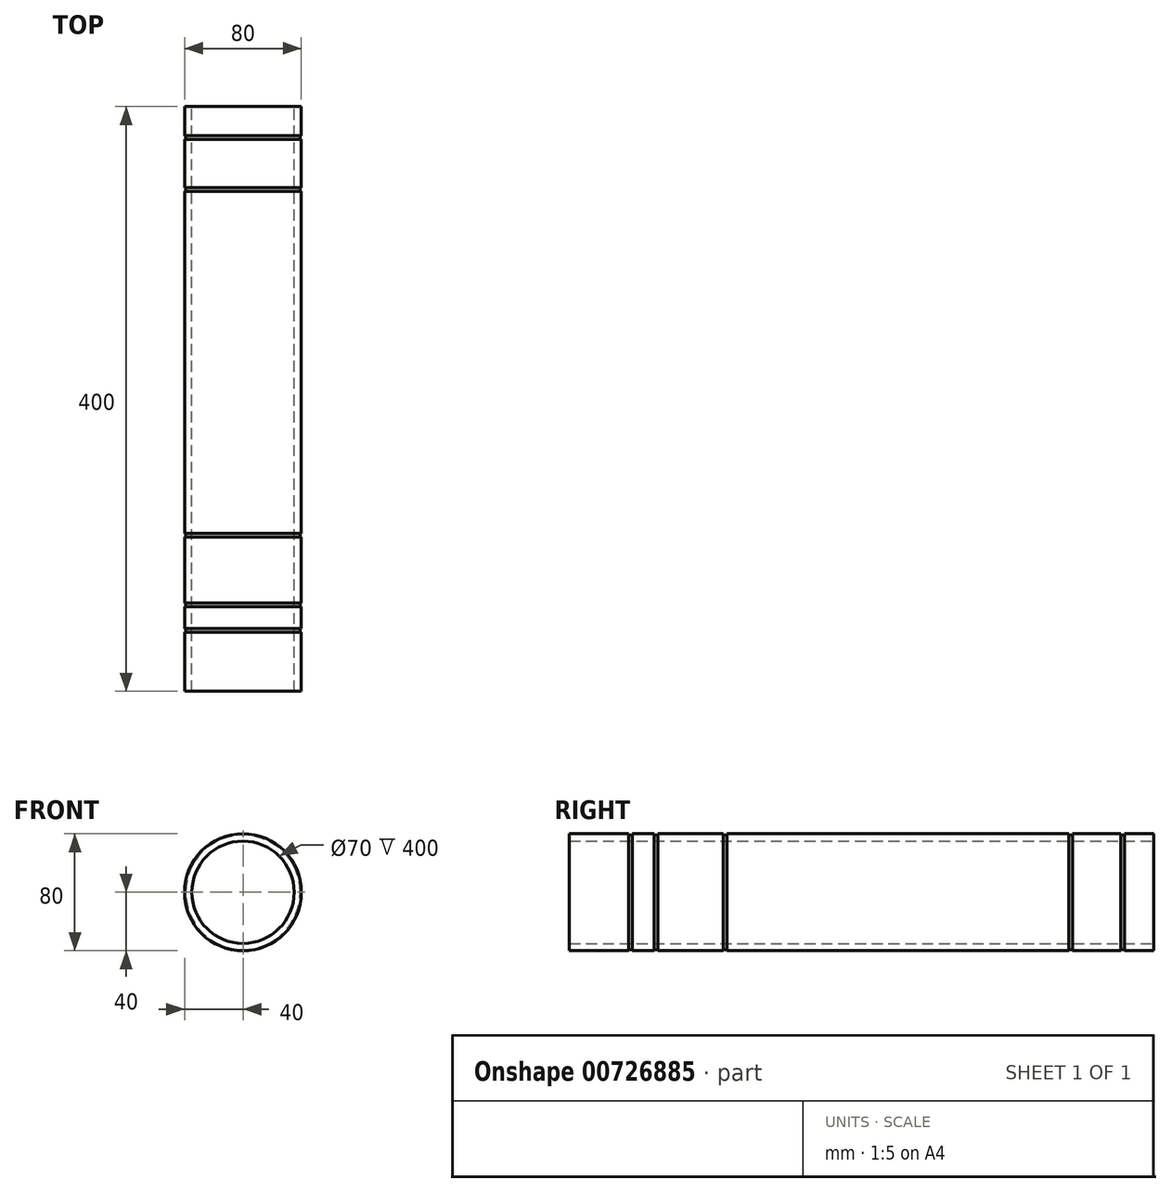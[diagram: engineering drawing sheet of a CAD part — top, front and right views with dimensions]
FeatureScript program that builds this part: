
annotation { "Feature Type Name" : "Feature", "Feature Type Description" : "" }
export const myFeature = defineFeature(function(context is Context, id is Id, definition is map)
    precondition{}
    {
        {
            var Q0;
            Q0=qCreatedBy(makeId("Front.planeOp"),FACE);
            var sketch = newSketch(context, id + "F0", { "sketchPlane" : qUnion([Q0])});
            skCircle(sketch, "E0", {"center": v(0, 0) * mm, "radius": 40 * mm});
            skCircle(sketch, "E1", {"center": v(0, 0) * mm, "radius": 35 * mm});
            skSolve(sketch);
        }
        {
            var Q0;
            Q0=makeQuery(id+"F0.imprint","IMPRINT",FACE,{"disambiguationData":[TD([[makeQuery(id+"F0.imprint","IMPRINT",EDGE,{"derivedFrom":sQuery(id+"F0.wireOp",EDGE,"E0")}),1.0]])]});
            extrude(context, id + "F1", {"entities" : qUnion([Q0]), "depth" : 400 * mm, "offsetDistance" : 25 * mm});
        }
        {
            var Q0;
            Q0=qCreatedBy(makeId("Front.planeOp"),FACE);
            cPlane(context, id + "F2", {"entities" : qUnion([Q0]), "cplaneType" : CPlaneType.OFFSET, "offset" : 20 * mm, "width" : 150 * mm, "height" : 150 * mm});
        }
        {
            var Q0;
            Q0=qCreatedBy(id+"F2.planeOp",FACE);
            var sketch = newSketch(context, id + "F3", { "sketchPlane" : qUnion([Q0])});
            skCircle(sketch, "E2", {"center": v(0, 0) * mm, "radius": 39.15 * mm});
            skCircle(sketch, "E3", {"center": v(0, 0) * mm, "radius": 44 * mm});
            skSolve(sketch);
        }
        {
            var Q0;
            Q0=qSketchRegion(id+"F3",true);
            extrude(context, id + "F4", {"entities" : qUnion([Q0]), "operationType" : NewBodyOperationType.REMOVE, "depth" : 2.5 * mm, "offsetDistance" : 25 * mm});
        }
        {
            var Q0;
            Q0=qCreatedBy(id+"F2.planeOp",FACE);
            cPlane(context, id + "F5", {"entities" : qUnion([Q0]), "cplaneType" : CPlaneType.OFFSET, "offset" : 35.5 * mm, "width" : 150 * mm, "height" : 150 * mm});
        }
        {
            var Q0;
            Q0=qCreatedBy(id+"F5.planeOp",FACE);
            var sketch = newSketch(context, id + "F6", { "sketchPlane" : qUnion([Q0])});
            skCircle(sketch, "E4", {"center": v(0, 0) * mm, "radius": 39.15 * mm});
            skCircle(sketch, "E5", {"center": v(0, 0) * mm, "radius": 42.5 * mm});
            skSolve(sketch);
        }
        {
            var Q0;
            Q0=qSketchRegion(id+"F6",true);
            extrude(context, id + "F7", {"entities" : qUnion([Q0]), "operationType" : NewBodyOperationType.REMOVE, "depth" : 2.5 * mm, "offsetDistance" : 25 * mm});
        }
        {
            var Q0;
            Q0=qCreatedBy(id+"F5.planeOp",FACE);
            cPlane(context, id + "F8", {"entities" : qUnion([Q0]), "cplaneType" : CPlaneType.OFFSET, "offset" : 444.5 * mm, "width" : 150 * mm, "height" : 150 * mm});
        }
        {
            var Q0;
            Q0=qCreatedBy(id+"F8.planeOp",FACE);
            cPlane(context, id + "F9", {"entities" : qUnion([Q0]), "cplaneType" : CPlaneType.OFFSET, "offset" : 20 * mm, "oppositeDirection" : true, "width" : 150 * mm, "height" : 150 * mm});
        }
        {
            var Q0;
            Q0=qCreatedBy(id+"F9.planeOp",FACE);
            var sketch = newSketch(context, id + "F10", { "sketchPlane" : qUnion([Q0])});
            skCircle(sketch, "E6", {"center": v(0, 0) * mm, "radius": 39.15 * mm});
            skCircle(sketch, "E7", {"center": v(0, 0) * mm, "radius": 42.5 * mm});
            skSolve(sketch);
        }
        {
            var Q0;
            Q0=qSketchRegion(id+"F10",true);
            extrude(context, id + "F11", {"entities" : qUnion([Q0]), "operationType" : NewBodyOperationType.REMOVE, "oppositeDirection" : true, "depth" : 2.5 * mm, "offsetDistance" : 25 * mm});
        }
        {
            var Q0;
            Q0=qCreatedBy(id+"F9.planeOp",FACE);
            cPlane(context, id + "F12", {"entities" : qUnion([Q0]), "cplaneType" : CPlaneType.OFFSET, "offset" : 35.5 * mm, "oppositeDirection" : true, "width" : 150 * mm, "height" : 150 * mm});
        }
        {
            var Q0;
            Q0=qCreatedBy(id+"F12.planeOp",FACE);
            var sketch = newSketch(context, id + "F13", { "sketchPlane" : qUnion([Q0])});
            skCircle(sketch, "E8", {"center": v(0, 0) * mm, "radius": 39.15 * mm});
            skCircle(sketch, "E9", {"center": v(0, 0) * mm, "radius": 42.5 * mm});
            skSolve(sketch);
        }
        {
            var Q0;
            Q0=qSketchRegion(id+"F13",true);
            extrude(context, id + "F14", {"entities" : qUnion([Q0]), "operationType" : NewBodyOperationType.REMOVE, "oppositeDirection" : true, "depth" : 2.5 * mm, "offsetDistance" : 25 * mm});
        }
        {
            var Q0;
            Q0=qCreatedBy(makeId("Front.planeOp"),FACE);
            cPlane(context, id + "F15", {"entities" : qUnion([Q0]), "cplaneType" : CPlaneType.OFFSET, "offset" : 590 * mm, "width" : 150 * mm, "height" : 150 * mm});
        }
        {
            var Q0;
            Q0=qCreatedBy(id+"F15.planeOp",FACE);
            var sketch = newSketch(context, id + "F16", { "sketchPlane" : qUnion([Q0])});
            skCircle(sketch, "E10", {"center": v(0, 0) * mm, "radius": 39.15 * mm});
            skCircle(sketch, "E11", {"center": v(0, 0) * mm, "radius": 44 * mm});
            skSolve(sketch);
        }
        {
            var Q0;
            Q0=qSketchRegion(id+"F16",true);
            extrude(context, id + "F17", {"entities" : qUnion([Q0]), "operationType" : NewBodyOperationType.REMOVE, "oppositeDirection" : true, "depth" : 2.5 * mm, "offsetDistance" : 25 * mm});
        }
        {
            var Q0;
            Q0=qCreatedBy(id+"F15.planeOp",FACE);
            cPlane(context, id + "F18", {"entities" : qUnion([Q0]), "cplaneType" : CPlaneType.OFFSET, "offset" : 10 * mm, "width" : 150 * mm, "height" : 150 * mm});
        }
        {
            var Q0;
            Q0=qCreatedBy(id+"F18.planeOp",FACE);
            var sketch = newSketch(context, id + "F19", { "sketchPlane" : qUnion([Q0])});
            skCircle(sketch, "E12", {"center": v(0, 0) * mm, "radius": 39.15 * mm});
            skCircle(sketch, "E13", {"center": v(0, 0) * mm, "radius": 44 * mm});
            skSolve(sketch);
        }
        {
            var Q0;
            Q0=qSketchRegion(id+"F19",true);
            extrude(context, id + "F20", {"entities" : qUnion([Q0]), "operationType" : NewBodyOperationType.REMOVE, "oppositeDirection" : true, "depth" : 2.5 * mm, "offsetDistance" : 25 * mm});
        }
        {
            var Q0;
            Q0=qCreatedBy(id+"F12.planeOp",FACE);
            cPlane(context, id + "F21", {"entities" : qUnion([Q0]), "cplaneType" : CPlaneType.OFFSET, "offset" : 150 * mm, "oppositeDirection" : true, "width" : 150 * mm, "height" : 150 * mm});
        }
        {
            var Q0;
            Q0=qCreatedBy(id+"F21.planeOp",FACE);
            var sketch = newSketch(context, id + "F22", { "sketchPlane" : qUnion([Q0])});
            skCircle(sketch, "E14", {"center": v(0, 0) * mm, "radius": 39.15 * mm});
            skCircle(sketch, "E15", {"center": v(0, 0) * mm, "radius": 42.5 * mm});
            skSolve(sketch);
        }
        {
            var Q0;
            Q0=makeQuery(id+"F22.imprint","IMPRINT",FACE,{"disambiguationData":[TD([[makeQuery(id+"F22.imprint","IMPRINT",EDGE,{"derivedFrom":sQuery(id+"F22.wireOp",EDGE,"E14")}),-1.0]])]});
            extrude(context, id + "F23", {"entities" : qUnion([Q0]), "operationType" : NewBodyOperationType.REMOVE, "oppositeDirection" : true, "depth" : 2.5 * mm, "offsetDistance" : 25 * mm});
        }
        {
            var Q0;
            Q0=qCreatedBy(id+"F12.planeOp",FACE);
            cPlane(context, id + "F24", {"entities" : qUnion([Q0]), "cplaneType" : CPlaneType.OFFSET, "offset" : 87.5 * mm, "oppositeDirection" : true, "width" : 150 * mm, "height" : 150 * mm});
        }
        {
            var Q0;
            Q0=qCreatedBy(id+"F24.planeOp",FACE);
            var sketch = newSketch(context, id + "F25", { "sketchPlane" : qUnion([Q0])});
            skCircle(sketch, "E16", {"center": v(0, 0) * mm, "radius": 39.15 * mm});
            skCircle(sketch, "E17", {"center": v(0, 0) * mm, "radius": 44 * mm});
            skSolve(sketch);
        }
        {
            var Q0;
            Q0=makeQuery(id+"F25.imprint","IMPRINT",FACE,{"disambiguationData":[TD([[makeQuery(id+"F25.imprint","IMPRINT",EDGE,{"derivedFrom":sQuery(id+"F25.wireOp",EDGE,"E16")}),-1.0]])]});
            extrude(context, id + "F26", {"entities" : qUnion([Q0]), "operationType" : NewBodyOperationType.REMOVE, "depth" : 2.5 * mm, "offsetDistance" : 25 * mm});
        }
        {
            var Q0;
            Q0=qCreatedBy(id+"F24.planeOp",FACE);
            cPlane(context, id + "F27", {"entities" : qUnion([Q0]), "cplaneType" : CPlaneType.OFFSET, "offset" : 17.5 * mm, "oppositeDirection" : true, "width" : 150 * mm, "height" : 150 * mm});
        }
        {
            var Q0;
            Q0=qCreatedBy(id+"F27.planeOp",FACE);
            var sketch = newSketch(context, id + "F28", { "sketchPlane" : qUnion([Q0])});
            skCircle(sketch, "E18", {"center": v(0, 0) * mm, "radius": 39.15 * mm});
            skCircle(sketch, "E19", {"center": v(0, 0) * mm, "radius": 44 * mm});
            skSolve(sketch);
        }
        {
            var Q0;
            Q0=makeQuery(id+"F28.imprint","IMPRINT",FACE,{"disambiguationData":[TD([[makeQuery(id+"F28.imprint","IMPRINT",EDGE,{"derivedFrom":sQuery(id+"F28.wireOp",EDGE,"E18")}),-1.0]])]});
            extrude(context, id + "F29", {"entities" : qUnion([Q0]), "operationType" : NewBodyOperationType.REMOVE, "depth" : 2.5 * mm, "offsetDistance" : 25 * mm});
        }
    });
